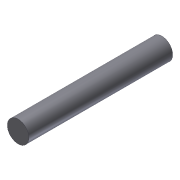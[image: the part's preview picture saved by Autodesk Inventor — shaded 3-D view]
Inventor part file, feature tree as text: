
AUTODESK INVENTOR PART (.ipt)
format: ipt  version: 2012 (Build 160160000, 160)  size: 69,120 bytes
history: native  units: in
note: dims shown in document units (in); Inventor stores cm internally (conversion verified against a paired STEP export)
features: extrude x1, sketch x1
ambient origin geometry x8: Origin, YZ Plane, XZ Plane, XY Plane, X Axis, Y Axis, Z Axis, Center Point
bodies: Solid1 (feature_tree)
feature tree (2):
  extrude  "Extrusion1"  Depth=2.5in TaperAngle=0.0deg
  sketch  "Sketch1"  dims[d0=0.375in d1=2.5in d2=0.0in]
